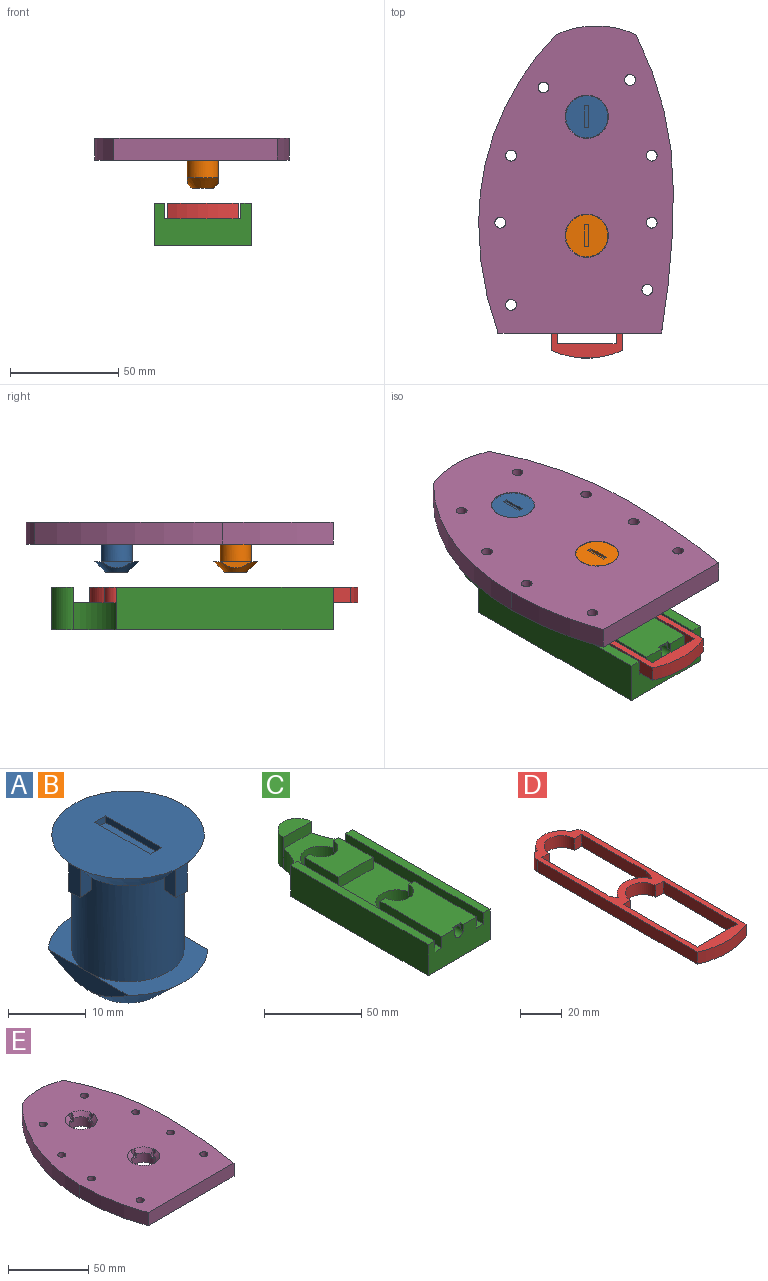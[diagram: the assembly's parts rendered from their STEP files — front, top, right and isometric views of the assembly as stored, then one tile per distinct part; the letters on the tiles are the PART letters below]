
ASSEMBLY  parts=5 mates=5
PART A: 34 faces, bbox 20.4x20.4x22.9 mm
  f0: cone r=7.2mm half-angle=41.9deg, axis (0,0,1), area 182.7mm2, adj f1,f6,f14,f15,f16,f17,f19,f20
  f1: plane 19.57x19.57mm, normal (0,0,1), area 280.8mm2, adj f0,f9,f10,f11,f12
  f2: cone r=5mm half-angle=46.8deg, axis (0,0,1), area 258.5mm2, adj f3,f4,f5,f7,f8
  f3: plane 14.4x10.2mm, normal (0,0,1), area 52.1mm2, adj f2,f6,f7,f8
  f4: plane 14.4x10.2mm, normal (0,0,1), area 52.1mm2, adj f2,f6,f7,f8
  f5: plane 10x10mm, normal (0,0,-1), area 78.5mm2, adj f2
  f6: cylinder r=7.2mm len=15.12mm, axis (0,0,1), area 684.2mm2, adj f0,f3,f4
  f7: plane 14.46x2.82mm, normal (1,0,0), area 26.1mm2, adj f2,f3,f4
  f8: plane 14.46x2.82mm, normal (-1,0,0), area 26.1mm2, adj f2,f3,f4
  f9: plane 10x1mm, normal (-1,0,0.05), area 10mm2, adj f1,f10,f12,f13
  f10: plane 2x1mm, normal (0,-1,0.05), area 2mm2, adj f1,f9,f11,f13
  f11: plane 10x1mm, normal (1,0,0.05), area 10mm2, adj f1,f10,f12,f13
  f12: plane 2x1mm, normal (0,1,0.05), area 2mm2, adj f1,f9,f11,f13
  f13: plane 9.9x1.9mm, normal (0,0,1), area 18.8mm2, adj f9,f10,f11,f12
  f14: cylinder r=7.5mm len=1.96mm, axis (0,0,1), area 3mm2, adj f0,f15,f17,f18
  f15: plane 4.47x2.25mm, normal (0.1,0.99,0), area 7.3mm2, adj f0,f14,f16,f18
  f16: plane 4.48x2.01mm, normal (-1,0,0), area 8.9mm2, adj f0,f15,f17,f18
  f17: plane 4.47x2.25mm, normal (0.1,-0.99,0), area 7.3mm2, adj f0,f14,f16,f18
  f18: plane 2.25x2mm, normal (0,0,-1), area 3.9mm2, adj f14,f15,f16,f17
  f19: plane 4.48x2.01mm, normal (0,1,0), area 8.9mm2, adj f0,f20,f22,f23
  f20: plane 4.47x2.25mm, normal (-0.99,-0.1,0), area 7.3mm2, adj f0,f19,f21,f23
  f21: cylinder r=7.5mm len=1.96mm, axis (0,0,1), area 3mm2, adj f0,f20,f22,f23
  f22: plane 4.47x2.25mm, normal (0.99,-0.1,0), area 7.3mm2, adj f0,f19,f21,f23
  f23: plane 2.25x2mm, normal (0,0,-1), area 3.9mm2, adj f19,f20,f21,f22
  f24: plane 4.47x2.25mm, normal (-0.1,0.99,0), area 7.3mm2, adj f0,f25,f27,f28
  f25: cylinder r=7.5mm len=1.96mm, axis (0,0,1), area 3mm2, adj f0,f24,f26,f28
  f26: plane 4.47x2.25mm, normal (-0.1,-0.99,0), area 7.3mm2, adj f0,f25,f27,f28
  f27: plane 4.52x2.04mm, normal (1,0,0), area 8.9mm2, adj f0,f24,f26,f28
  f28: plane 2.25x2mm, normal (0,0,-1), area 3.9mm2, adj f24,f25,f26,f27
  f29: plane 4.48x2.01mm, normal (0,-1,0), area 8.9mm2, adj f0,f30,f32,f33
  f30: plane 4.47x2.25mm, normal (0.99,0.1,0), area 7.3mm2, adj f0,f29,f31,f33
  f31: cylinder r=7.5mm len=1.96mm, axis (0,0,1), area 3mm2, adj f0,f30,f32,f33
  f32: plane 4.47x2.25mm, normal (-0.99,0.1,0), area 7.3mm2, adj f0,f29,f31,f33
  f33: plane 2.25x2mm, normal (0,0,-1), area 3.9mm2, adj f29,f30,f31,f32
PART B: same geometry as A
PART C: 40 faces, bbox 45x130x19.5 mm
  f0: plane 45x19.5mm, normal (0,-1,0), area 772.4mm2, adj f1,f4,f5,f7,f15,f16,f20,f28
  f1: plane 120x45mm, normal (0,0,1), area 1939.4mm2, adj f0,f3,f4,f5,f6,f9,f10,f11
  f2: cylinder r=8.5mm len=17mm, axis (0,0,1), area 186.9mm2, adj f3,f6,f7,f24
  f3: plane 7x4mm, normal (0,1,0), area 28mm2, adj f1,f2,f4,f7,f24
  f4: plane 45x7mm, normal (1,0,0), area 315mm2, adj f0,f1,f3,f7
  f5: plane 45x7mm, normal (-1,0,0), area 315mm2, adj f0,f1,f6,f7
  f6: plane 7x4mm, normal (0,1,0), area 28mm2, adj f1,f2,f5,f7,f24
  f7: plane 45x25mm, normal (0,0,1), area 999.5mm2, adj f0,f2,f3,f4,f5,f6,f37,f38
  f8: cylinder r=8.5mm len=17mm, axis (0,0,1), area 186.9mm2, adj f9,f13,f14,f23
  f9: plane 7x4mm, normal (0,1,0), area 28mm2, adj f1,f8,f10,f14,f23
  f10: plane 25x7mm, normal (1,0,0), area 175mm2, adj f1,f9,f11,f14
  f11: plane 25x7mm, normal (0,-1,0), area 175mm2, adj f1,f10,f12,f14
  f12: plane 25x7mm, normal (-1,0,0), area 175mm2, adj f1,f11,f13,f14
  f13: plane 7x4mm, normal (0,1,0), area 28mm2, adj f1,f8,f12,f14,f23
  f14: plane 25x25mm, normal (0,0,1), area 511.5mm2, adj f8,f9,f10,f11,f12,f13
  f15: plane 100x19.5mm, normal (1,0,0), area 1950mm2, adj f0,f19,f20,f27,f29
  f16: plane 100x19.5mm, normal (-1,0,0), area 1950mm2, adj f0,f17,f20,f30,f32
  f17: cylinder r=25mm len=20mm, axis (0,0,1), area 327.2mm2, adj f1,f16,f18,f20
  f18: cylinder r=10mm len=20mm, axis (0,0,1), area 612.6mm2, adj f17,f19,f20,f33,f34
  f19: cylinder r=40mm len=20mm, axis (0,0,1), area 283.3mm2, adj f1,f15,f18,f20
  f20: plane 130x45mm, normal (0,0,-1), area 5226.6mm2, adj f0,f15,f16,f17,f18,f19
  f21: cylinder r=11mm len=22mm, axis (0,0,1), area 552.9mm2, adj f1,f22,f23
  f22: plane 22x22mm, normal (0,0,1), area 380.1mm2, adj f21
  f23: plane 22x11mm, normal (0,0,-1), area 76.6mm2, adj f8,f9,f13,f21
  f24: plane 22x11mm, normal (0,0,-1), area 76.6mm2, adj f2,f3,f6,f25
  f25: cylinder r=11mm len=22mm, axis (0,0,1), area 552.9mm2, adj f1,f24,f26
  f26: plane 22x22mm, normal (0,0,1), area 380.1mm2, adj f25
  f27: plane 7x5mm, normal (0,1,0), area 35mm2, adj f1,f15,f28,f29
  f28: plane 100x7mm, normal (-1,0,0), area 700mm2, adj f0,f1,f27,f29
  f29: plane 100x5mm, normal (0,0,1), area 500mm2, adj f0,f15,f27,f28
  f30: plane 7x5mm, normal (0,1,0), area 35mm2, adj f1,f16,f31,f32
  f31: plane 100x7mm, normal (1,0,0), area 700mm2, adj f0,f1,f30,f32
  f32: plane 100x5mm, normal (0,0,1), area 500mm2, adj f0,f16,f30,f31
  f33: plane 20x7mm, normal (0,-1,0), area 140mm2, adj f1,f18,f34
  f34: plane 20x10mm, normal (0,0,1), area 157.1mm2, adj f18,f33
  f35: cylinder r=3mm len=7mm, axis (0,-1,0), area 113.1mm2, adj f0,f36,f37,f38,f39
  f36: plane 6x6mm, normal (0,-1,0), area 28.3mm2, adj f35
  f37: plane 3.5x2mm, normal (1,0,0), area 7mm2, adj f0,f7,f35,f39
  f38: plane 3.5x2mm, normal (-1,0,0), area 7mm2, adj f0,f7,f35,f39
  f39: plane 6x3.5mm, normal (0,-1,0), area 6.9mm2, adj f7,f35,f37,f38
PART D: 24 faces, bbox 33x124.1x7 mm
  f0: plane 7x5mm, normal (0,-1,0), area 35mm2, adj f1,f19,f20,f21
  f1: plane 43.45x7mm, normal (1,0,0), area 304.1mm2, adj f0,f2,f20,f21
  f2: cylinder r=8.97mm len=7mm, axis (0,0,1), area 46mm2, adj f1,f3,f20,f21
  f3: cylinder r=12.5mm len=22.4mm, axis (0,0,1), area 194.3mm2, adj f2,f4,f20,f21
  f4: cylinder r=8.97mm len=7mm, axis (0,0,1), area 46mm2, adj f3,f5,f20,f21
  f5: plane 43.45x7mm, normal (-1,0,0), area 304.1mm2, adj f4,f6,f20,f21
  f6: plane 7x5mm, normal (0,-1,0), area 35mm2, adj f5,f19,f20,f21
  f7: cylinder r=8.5mm len=17mm, axis (0,0,1), area 186.9mm2, adj f8,f17,f20,f21
  f8: plane 7x5mm, normal (0,-1,0), area 35mm2, adj f7,f9,f20,f21
  f9: plane 50x7mm, normal (1,0,0), area 350mm2, adj f8,f10,f20,f21
  f10: plane 27x7mm, normal (0,1,0), area 160.7mm2, adj f9,f11,f20,f21,f22
  f11: plane 50x7mm, normal (-1,0,0), area 350mm2, adj f10,f17,f20,f21
  f12: cylinder r=5.56mm len=7mm, axis (0,0,1), area 59.3mm2, adj f13,f18,f20,f21
  f13: cylinder r=12.5mm len=22.4mm, axis (0,0,1), area 194.3mm2, adj f12,f14,f20,f21
  f14: cylinder r=5.56mm len=7mm, axis (0,0,1), area 59.3mm2, adj f13,f15,f20,f21
  f15: plane 108x7mm, normal (1,0,0), area 756mm2, adj f14,f16,f20,f21
  f16: cylinder r=40mm len=33mm, axis (0,0,1), area 238.1mm2, adj f15,f18,f20,f21
  f17: plane 7x5mm, normal (0,-1,0), area 35mm2, adj f7,f11,f20,f21
  f18: plane 108x7mm, normal (-1,0,0), area 756mm2, adj f12,f16,f20,f21
  f19: cylinder r=8.5mm len=17mm, axis (0,0,1), area 186.9mm2, adj f0,f6,f20,f21
  f20: plane 124.06x33mm, normal (0,0,-1), area 1132.4mm2, adj f0,f1,f2,f3,f4,f5,f6,f7
  f21: plane 124.06x33mm, normal (0,0,1), area 1132.4mm2, adj f0,f1,f2,f3,f4,f5,f6,f7
  f22: cylinder r=3mm len=6mm, axis (0,1,0), area 56.5mm2, adj f10,f23
  f23: plane 6x6mm, normal (0,1,0), area 28.3mm2, adj f22
PART E: 66 faces, bbox 90x142x10 mm
  f0: cylinder r=7.5mm len=15mm, axis (0,0,1), area 316.5mm2, adj f1,f2,f3,f4,f32,f50,f52,f53
  f1: cone r=7.5mm half-angle=41deg, axis (0,0,1), area 42.3mm2, adj f0,f31,f52,f62
  f2: cone r=7.5mm half-angle=41deg, axis (0,0,1), area 42.3mm2, adj f0,f31,f54,f64
  f3: cone r=7.5mm half-angle=41deg, axis (0,0,1), area 42.3mm2, adj f0,f31,f56,f58
  f4: cone r=7.5mm half-angle=41deg, axis (0,0,1), area 42.3mm2, adj f0,f31,f50,f60
  f5: cone r=7.5mm half-angle=41deg, axis (0,0,1), area 0.3mm2, adj f31,f63
  f6: cone r=7.5mm half-angle=41deg, axis (0,0,1), area 0.3mm2, adj f31,f59
  f7: cone r=7.5mm half-angle=41deg, axis (0,0,1), area 0.3mm2, adj f31,f55
  f8: cylinder r=7.5mm len=15mm, axis (0,0,1), area 316.5mm2, adj f9,f11,f13,f14,f32,f35,f36,f37
  f9: cone r=7.5mm half-angle=41deg, axis (0,0,1), area 42.3mm2, adj f8,f31,f43,f46
  f10: cone r=7.5mm half-angle=41deg, axis (0,0,1), area 0.3mm2, adj f31,f47
  f11: cone r=7.5mm half-angle=41deg, axis (0,0,1), area 42.3mm2, adj f8,f31,f36,f48
  f12: cone r=7.5mm half-angle=41deg, axis (0,0,1), area 0.3mm2, adj f31,f42
  f13: cone r=7.5mm half-angle=41deg, axis (0,0,1), area 42.3mm2, adj f8,f31,f38,f44
  f14: cone r=7.5mm half-angle=41deg, axis (0,0,1), area 42.3mm2, adj f8,f31,f35,f39
  f15: cone r=7.5mm half-angle=41deg, axis (0,0,1), area 0.3mm2, adj f31,f40
  f16: cone r=7.5mm half-angle=41deg, axis (0,0,1), area 0.3mm2, adj f31,f34
  f17: cylinder r=150mm len=51mm, axis (0,0,-1), area 520.4mm2, adj f18,f30,f31,f32
  f18: plane 75.58x10mm, normal (0,-1,0), area 755.8mm2, adj f17,f19,f31,f32
  f19: cylinder r=400mm len=66mm, axis (0,0,-1), area 663mm2, adj f18,f20,f31,f32
  f20: cylinder r=158mm len=72mm, axis (0,0,-1), area 747.6mm2, adj f19,f21,f31,f32
  f21: cylinder r=44mm len=36.66mm, axis (0,0,-1), area 378.1mm2, adj f20,f30,f31,f32
  f22: cylinder r=2.5mm len=10mm, axis (0,0,-1), area 157.1mm2, adj f31,f32
  f23: cylinder r=2.5mm len=10mm, axis (0,0,-1), area 157.1mm2, adj f31,f32
  f24: cylinder r=2.5mm len=10mm, axis (0,0,-1), area 157.1mm2, adj f31,f32
  f25: cylinder r=2.5mm len=10mm, axis (0,0,-1), area 157.1mm2, adj f31,f32
  f26: cylinder r=2.5mm len=10mm, axis (0,0,-1), area 157.1mm2, adj f31,f32
  f27: cylinder r=2.5mm len=10mm, axis (0,0,-1), area 157.1mm2, adj f31,f32
  f28: cylinder r=2.5mm len=10mm, axis (0,0,-1), area 157.1mm2, adj f31,f32
  f29: cylinder r=2.5mm len=10mm, axis (0,0,-1), area 157.1mm2, adj f31,f32
  f30: cylinder r=123.17mm len=87mm, axis (0,0,-1), area 966mm2, adj f17,f21,f31,f32
  f31: plane 142x90mm, normal (0,0,1), area 10082.2mm2, adj f1,f2,f3,f4,f5,f6,f7,f9
  f32: plane 142x90mm, normal (0,0,-1), area 10357.1mm2, adj f0,f8,f17,f18,f19,f20,f21,f22
  f33: cone r=7.5mm half-angle=41deg, axis (0,0,1), area 0.3mm2, adj f31,f51
  f34: plane 5.01x3.01mm, normal (0,1,0), area 14.7mm2, adj f16,f35,f36,f37
  f35: plane 5x2.47mm, normal (-0.99,-0.15,0), area 8.9mm2, adj f8,f14,f34,f37
  f36: plane 5x2.47mm, normal (0.99,-0.15,0), area 8.9mm2, adj f8,f11,f34,f37
  f37: plane 3x2.47mm, normal (0,0,1), area 6.4mm2, adj f8,f34,f35,f36
  f38: plane 5x2.47mm, normal (0.15,-0.99,0), area 8.9mm2, adj f8,f13,f40,f41
  f39: plane 5x2.47mm, normal (0.15,0.99,0), area 8.9mm2, adj f8,f14,f40,f41
  f40: plane 5.01x3.01mm, normal (-1,0,0), area 14.7mm2, adj f15,f38,f39,f41
  f41: plane 3x2.47mm, normal (0,0,1), area 6.4mm2, adj f8,f38,f39,f40
  f42: plane 5.01x3.01mm, normal (0,-1,0), area 14.7mm2, adj f12,f43,f44,f45
  f43: plane 5x2.47mm, normal (0.99,0.15,0), area 8.9mm2, adj f8,f9,f42,f45
  f44: plane 5x2.47mm, normal (-0.99,0.15,0), area 8.9mm2, adj f8,f13,f42,f45
  f45: plane 3x2.47mm, normal (0,0,1), area 6.4mm2, adj f8,f42,f43,f44
  f46: plane 5x2.47mm, normal (-0.15,-0.99,0), area 8.9mm2, adj f8,f9,f47,f49
  f47: plane 5.01x3.01mm, normal (1,0,0), area 14.7mm2, adj f10,f46,f48,f49
  f48: plane 5x2.47mm, normal (-0.15,0.99,0), area 8.9mm2, adj f8,f11,f47,f49
  f49: plane 3x2.47mm, normal (0,0,1), area 6.4mm2, adj f8,f46,f47,f48
  f50: plane 5x2.47mm, normal (-0.15,-0.99,0), area 8.9mm2, adj f0,f4,f51,f53
  f51: plane 5.01x3.01mm, normal (1,0,0), area 14.7mm2, adj f33,f50,f52,f53
  f52: plane 5x2.47mm, normal (-0.15,0.99,0), area 8.9mm2, adj f0,f1,f51,f53
  f53: plane 3x2.47mm, normal (0,0,1), area 6.4mm2, adj f0,f50,f51,f52
  f54: plane 5x2.47mm, normal (0.15,0.99,0), area 8.9mm2, adj f0,f2,f55,f57
  f55: plane 5.01x3.01mm, normal (-1,0,0), area 14.7mm2, adj f7,f54,f56,f57
  f56: plane 5x2.47mm, normal (0.15,-0.99,0), area 8.9mm2, adj f0,f3,f55,f57
  f57: plane 3x2.47mm, normal (0,0,1), area 6.4mm2, adj f0,f54,f55,f56
  f58: plane 5x2.47mm, normal (-0.99,0.15,0), area 8.9mm2, adj f0,f3,f59,f61
  f59: plane 5.01x3.01mm, normal (0,-1,0), area 14.7mm2, adj f6,f58,f60,f61
  f60: plane 5x2.47mm, normal (0.99,0.15,0), area 8.9mm2, adj f0,f4,f59,f61
  f61: plane 3x2.47mm, normal (0,0,1), area 6.4mm2, adj f0,f58,f59,f60
  f62: plane 5x2.47mm, normal (0.99,-0.15,0), area 8.9mm2, adj f0,f1,f63,f65
  f63: plane 5.01x3.01mm, normal (0,1,0), area 14.7mm2, adj f5,f62,f64,f65
  f64: plane 5x2.47mm, normal (-0.99,-0.15,0), area 8.9mm2, adj f0,f2,f63,f65
  f65: plane 3x2.47mm, normal (0,0,1), area 6.4mm2, adj f0,f62,f63,f64
PLACE A t=(3.27,55,-10.12)mm
PLACE B t=(3.27,0,-10.12)mm
PLACE C t=(3.27,0,30)mm
PLACE D t=(3.27,0,30)mm
PLACE E t=(3.27,0,-10)mm
MATE slider B.f0 <-> E.f0  axis (0,0,-1) through (3.27,45,-23)mm
MATE slider A.f0 <-> E.f8  axis (0,0,-1) through (3.27,100,-23)mm
MATE slider D.f8 <-> C.f6  axis (0,-1,0) through (-7.73,45,-33.5)mm
MATE slider C.f2 <-> E.f0  axis (0,0,1) through (3.27,45,-30)mm
MATE planar A.f0 <-> B.f0  axis (0,0,1) through (3.27,100,-0.12)mm
